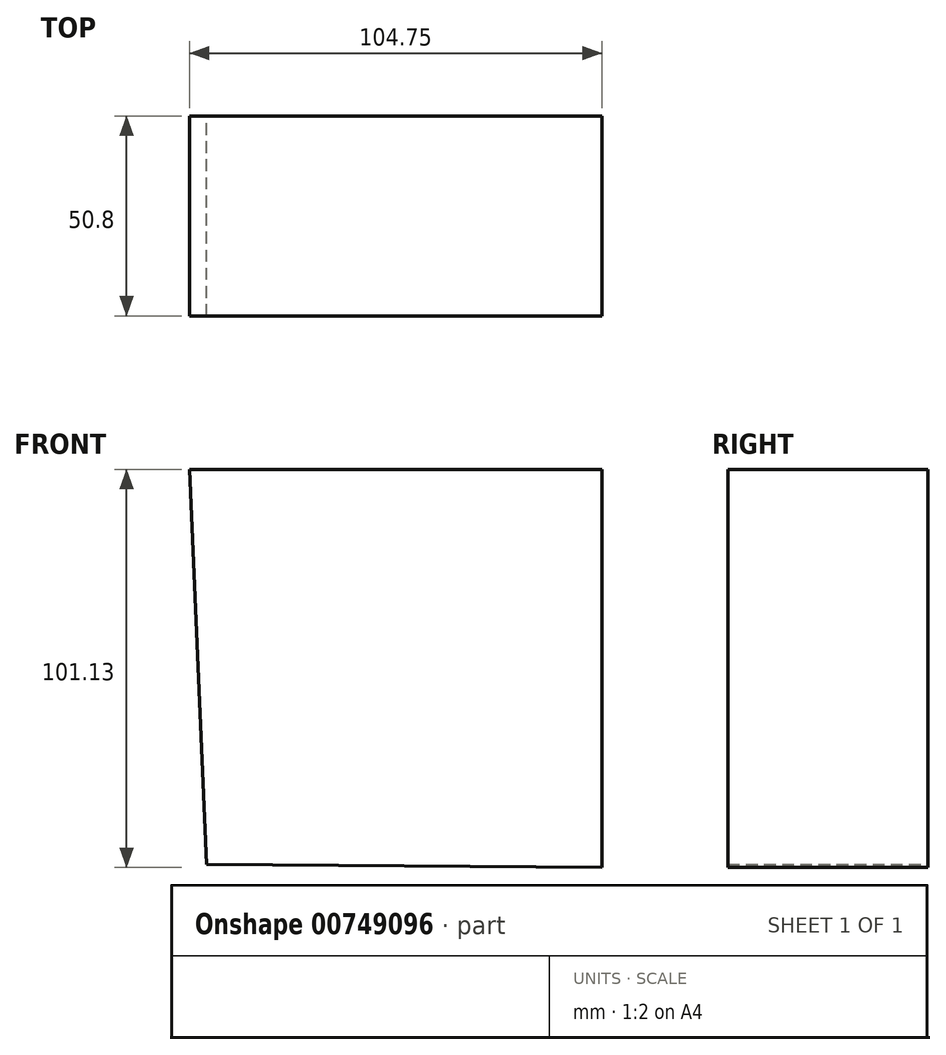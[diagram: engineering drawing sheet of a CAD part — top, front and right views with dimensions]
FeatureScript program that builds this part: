
annotation { "Feature Type Name" : "Feature", "Feature Type Description" : "" }
export const myFeature = defineFeature(function(context is Context, id is Id, definition is map)
    precondition{}
    {
        {
            var Q0;
            Q0=qCreatedBy(makeId("Front.planeOp"),FACE);
            var sketch = newSketch(context, id + "F0", { "sketchPlane" : qUnion([Q0])});
            skLineSegment(sketch, "E0", {"start": v(-62.9, 48.24) * mm, "end": v(41.85, 48.24) * mm});
            skLineSegment(sketch, "E1", {"start": v(41.85, 48.24) * mm, "end": v(41.85, -52.9) * mm});
            skLineSegment(sketch, "E2", {"start": v(41.85, -52.9) * mm, "end": v(-58.61, -52.13) * mm});
            skLineSegment(sketch, "E3", {"start": v(-58.61, -52.13) * mm, "end": v(-62.9, 48.24) * mm});
            skSolve(sketch);
        }
        {
            var Q0;
            Q0 = qSketchRegion(id + "F0", true);
            extrude(context, id + "F1", {"entities" : qUnion([Q0]), "depth" : 50.8 * mm, "offsetDistance" : 25.4 * mm});
        }
    });
